# Revit family: Air-Curtain_Climate-Control_PoweredAire_ECE-HW
name_source: partatom
category: Mechanical Equipment
units: mm (PartAtom-declared; Revit-internal decimal feet)

## family parameters
Cut with Voids When Loaded = No
Host = Face
Maintain Annotation Orientation = No
OmniClass Number = 23.75.35.17.21
OmniClass Title = Air Curtains
Part Type = Normal
Room Calculation Point = No
Round Connector Dimension = Use Diameter
Shared = No

## types (1)
- Air-Curtain_Climate-Control_PoweredAire_ECE-HW
    Assembly Code = D3090400
    Default Elevation = 0' - 0"
    HVAC_BTU Input = 0.0 Btu/h
    HVAC_Outlet Velocity Uniformity = 0
    Heating Element Load = 0 W
    Keynote = 23 34 33
    Manufacturer = Powered Aire, Inc
    Max Height = 0' - 0"
    Model = ECE HW
    Motor Count = 0
    Motor HP = 0
    Motor RPM = 0
    Mounting Width = 3' - 11 1/2"
    Nozzle Width = 3' - 10"
    Power Rating = 0 W
    Product Page URL = https://www.arcat.com
    URL = http://www.poweredaire.com
    Unit Height = 1' - 3"
    Unit Weight = 0
    Unit Width = 4' - 1"
    Unit Width Notes = Other Widths available.

## geometry (parser evidence)
native form markers: Sweep x2
no freeform markers — native parametric forms only
